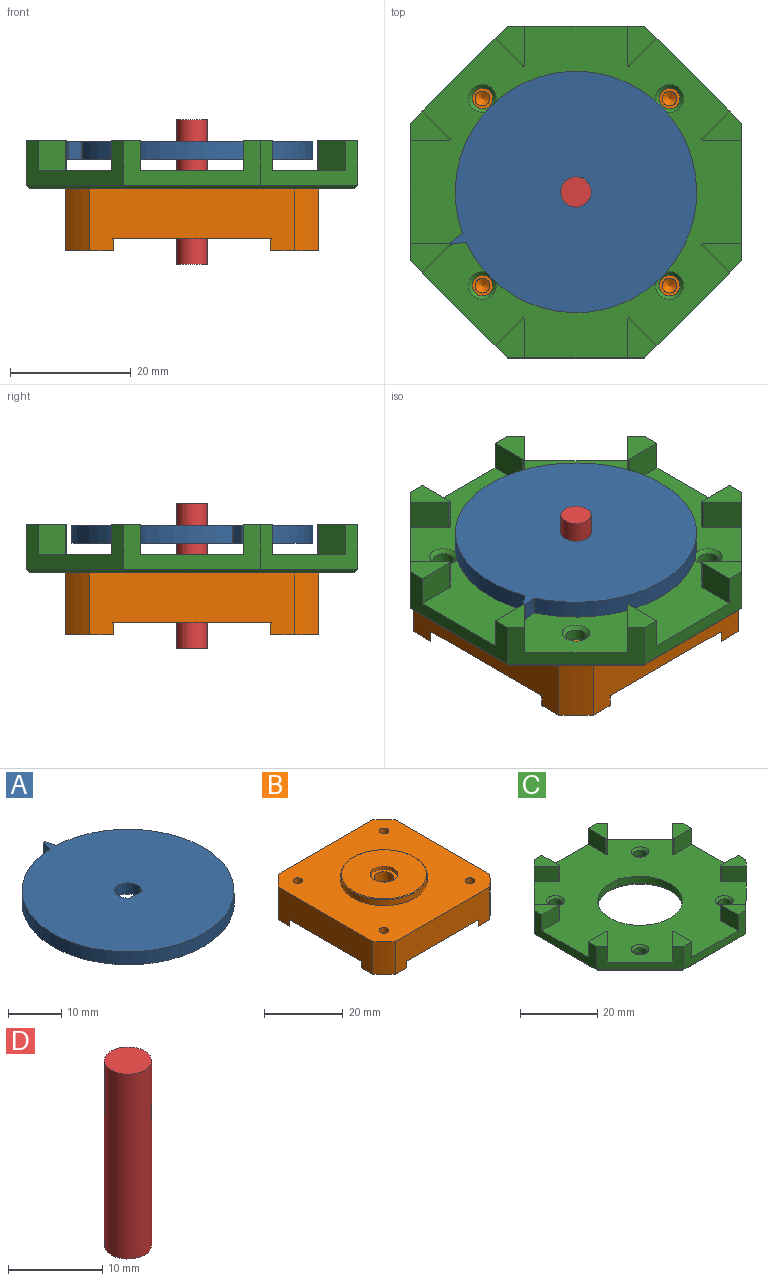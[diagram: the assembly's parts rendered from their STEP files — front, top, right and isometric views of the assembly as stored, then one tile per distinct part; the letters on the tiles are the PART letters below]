
ASSEMBLY  parts=4 mates=4
PART A: 14 faces, bbox 40x42.4x3 mm
  f0: plane 3x2.15mm, normal (0.97,0.26,0), area 6.7mm2, adj f6,f7,f8,f10
  f1: plane 3x2.15mm, normal (-0.97,0.26,0), area 6.7mm2, adj f6,f7,f8,f9
  f2: plane 3.23x2.4mm, normal (0,1,0), area 7.8mm2, adj f3,f4,f6,f11
  f3: cylinder r=2.5mm len=5mm, axis (0,0,-1), area 27.6mm2, adj f2,f4,f6,f12
  f4: plane 2.4x0.75mm, normal (-0.87,0.5,0), area 2.1mm2, adj f2,f3,f6,f13
  f5: cylinder r=20mm len=40mm, axis (0,0,-1), area 371.3mm2, adj f6,f7,f9,f10
  f6: plane 42.43x40mm, normal (0,0,1), area 1240.3mm2, adj f0,f1,f2,f3,f4,f5,f8,f9
  f7: plane 42.43x40mm, normal (0,0,-1), area 1229.8mm2, adj f0,f1,f5,f8,f9,f10,f11,f12
  f8: cylinder r=0.2mm len=3mm, axis (0,0,1), area 1.6mm2, adj f0,f1,f6,f7
  f9: cylinder r=0.2mm len=3mm, axis (0,0,-1), area 0.8mm2, adj f1,f5,f6,f7
  f10: cylinder r=0.2mm len=3mm, axis (0,0,-1), area 0.8mm2, adj f0,f5,f6,f7
  f11: plane 3.78x0.62mm, normal (0,0.71,-0.71), area 3mm2, adj f2,f7,f12,f13
  f12: cone r=3.1mm half-angle=45deg, axis (0,0,-1), area 11mm2, adj f3,f7,f11,f13
  f13: plane 1.35x0.95mm, normal (-0.61,0.35,-0.71), area 0.9mm2, adj f4,f7,f11,f12
PART B: 33 faces, bbox 42x42x12.2 mm
  f0: plane 8x8mm, normal (-0.71,0.71,0), area 22.6mm2, adj f4,f5,f9,f28
  f1: plane 8x8mm, normal (0.71,0.71,0), area 22.6mm2, adj f4,f8,f28,f30
  f2: plane 8x8mm, normal (0.71,-0.71,0), area 22.6mm2, adj f4,f7,f10,f30
  f3: plane 8x8mm, normal (-0.71,-0.71,0), area 22.6mm2, adj f4,f5,f6,f10
  f4: plane 42x42mm, normal (0,0,-1), area 1636mm2, adj f0,f1,f2,f3,f5,f10,f28,f30
  f5: plane 33.94x10.2mm, normal (1,0,0), area 294.2mm2, adj f0,f3,f4,f6,f9,f26,f27,f32
  f6: plane 8x8mm, normal (0,0,-1), area 24.5mm2, adj f3,f5,f10,f26
  f7: plane 8x8mm, normal (0,0,-1), area 24.5mm2, adj f2,f10,f30,f31
  f8: plane 8x8mm, normal (0,0,-1), area 24.5mm2, adj f1,f28,f29,f30
  f9: plane 8x8mm, normal (0,0,-1), area 24.5mm2, adj f0,f5,f27,f28
  f10: plane 33.94x10.2mm, normal (0,1,0), area 294.2mm2, adj f2,f3,f4,f6,f7,f26,f31,f32
  f11: cone r=10.9mm half-angle=45deg, axis (0,0,-1), area 19.4mm2, adj f12,f13
  f12: cylinder r=11mm len=22mm, axis (0,0,1), area 124.4mm2, adj f11,f32
  f13: plane 21.6x21.6mm, normal (0,0,1), area 328mm2, adj f11,f15
  f14: plane 7x7mm, normal (0,0,1), area 18.8mm2, adj f15,f16
  f15: cylinder r=3.5mm len=7mm, axis (0,0,1), area 22mm2, adj f13,f14
  f16: cylinder r=2.5mm len=5mm, axis (0,0,1), area 47.1mm2, adj f14,f17
  f17: plane 5x5mm, normal (0,0,1), area 19.6mm2, adj f16
  f18: cone r=0.61mm half-angle=59deg, axis (0,0,1), area 5.5mm2, adj f19
  f19: cylinder r=1.23mm len=2.5mm, axis (0,0,1), area 19.3mm2, adj f18,f32
  f20: cone r=0.61mm half-angle=59deg, axis (0,0,1), area 5.5mm2, adj f21
  f21: cylinder r=1.23mm len=2.5mm, axis (0,0,1), area 19.3mm2, adj f20,f32
  f22: cone r=0.61mm half-angle=59deg, axis (0,0,1), area 5.5mm2, adj f23
  f23: cylinder r=1.23mm len=2.5mm, axis (0,0,1), area 19.3mm2, adj f22,f32
  f24: cone r=0.61mm half-angle=59deg, axis (0,0,1), area 5.5mm2, adj f25
  f25: cylinder r=1.23mm len=2.5mm, axis (0,0,1), area 19.3mm2, adj f24,f32
  f26: cylinder r=27mm len=10.2mm, axis (0,0,1), area 58.2mm2, adj f5,f6,f10,f32
  f27: cylinder r=27mm len=10.2mm, axis (0,0,1), area 58.2mm2, adj f5,f9,f28,f32
  f28: plane 33.94x10.2mm, normal (0,-1,0), area 294.2mm2, adj f0,f1,f4,f8,f9,f27,f29,f32
  f29: cylinder r=27mm len=10.2mm, axis (0,0,1), area 58.2mm2, adj f8,f28,f30,f32
  f30: plane 33.94x10.2mm, normal (-1,0,0), area 294.2mm2, adj f1,f2,f4,f7,f8,f29,f31,f32
  f31: cylinder r=27mm len=10.2mm, axis (0,0,1), area 58.2mm2, adj f7,f10,f30,f32
  f32: plane 42x42mm, normal (0,0,1), area 1334.7mm2, adj f5,f10,f12,f19,f21,f23,f25,f26
PART C: 66 faces, bbox 55.3x55.3x8.3 mm
  f0: plane 55x55mm, normal (0,0,1), area 1899.9mm2, adj f2,f3,f4,f5,f6,f7,f8,f9
  f1: cone r=11.8mm half-angle=45deg, axis (0,0,-1), area 79.4mm2, adj f9,f11,f16,f17
  f2: plane 16.11x16.11mm, normal (0.71,-0.71,0), area 83.4mm2, adj f0,f3,f10,f22,f24,f27,f28,f56
  f3: plane 22.78x7.4mm, normal (1,0,0), area 83.4mm2, adj f0,f2,f4,f26,f28,f31,f32,f54
  f4: plane 16.11x16.11mm, normal (0.71,0.71,0), area 83.4mm2, adj f0,f3,f5,f30,f32,f35,f36,f52
  f5: plane 22.78x7.4mm, normal (0,1,0), area 83.4mm2, adj f0,f4,f6,f34,f36,f39,f40,f50
  f6: plane 16.11x16.11mm, normal (-0.71,0.71,0), area 83.4mm2, adj f0,f5,f7,f38,f40,f43,f44,f51
  f7: plane 22.78x7.4mm, normal (-1,0,0), area 83.4mm2, adj f0,f6,f8,f42,f44,f47,f48,f53
  f8: plane 16.11x16.11mm, normal (-0.71,-0.71,0), area 83.4mm2, adj f0,f7,f10,f19,f20,f46,f48,f55
  f9: cylinder r=11mm len=22mm, axis (0,0,-1), area 139.4mm2, adj f0,f1,f16,f17
  f10: plane 22.78x7.4mm, normal (0,-1,0), area 83.4mm2, adj f0,f2,f8,f18,f20,f23,f24,f57
  f11: plane 53.8x53.8mm, normal (0,0,-1), area 1893.9mm2, adj f1,f50,f51,f52,f53,f54,f55,f56
  f12: cylinder r=1.7mm len=3.4mm, axis (0,0,-1), area 19.2mm2, adj f61,f65
  f13: cylinder r=1.7mm len=3.4mm, axis (0,0,-1), area 19.2mm2, adj f59,f64
  f14: cylinder r=1.7mm len=3.4mm, axis (0,0,-1), area 19.2mm2, adj f58,f63
  f15: cylinder r=1.7mm len=3.4mm, axis (0,0,-1), area 19.2mm2, adj f60,f62
  f16: plane 3.24x2.87mm, normal (0,-1,0), area 6.9mm2, adj f0,f1,f9,f17
  f17: plane 2.86x2.83mm, normal (-0.5,-0.87,0), area 6.9mm2, adj f0,f1,f9,f16
  f18: plane 6.45x5mm, normal (1,0,0), area 32.2mm2, adj f0,f10,f20,f21
  f19: plane 5x4.56mm, normal (-0.71,0.71,0), area 32.2mm2, adj f0,f8,f20,f21
  f20: plane 6.65x4.9mm, normal (0,0,1), area 19.8mm2, adj f8,f10,f18,f19,f21
  f21: cylinder r=0.2mm len=5mm, axis (0,0,-1), area 2.4mm2, adj f0,f18,f19,f20
  f22: plane 5x4.56mm, normal (0.71,0.71,0), area 32.2mm2, adj f0,f2,f24,f25
  f23: plane 6.45x5mm, normal (-1,0,0), area 32.2mm2, adj f0,f10,f24,f25
  f24: plane 6.65x4.9mm, normal (0,0,1), area 19.8mm2, adj f2,f10,f22,f23,f25
  f25: cylinder r=0.2mm len=5mm, axis (0,0,-1), area 2.4mm2, adj f0,f22,f23,f24
  f26: plane 6.45x5mm, normal (0,1,0), area 32.2mm2, adj f0,f3,f28,f29
  f27: plane 5x4.56mm, normal (-0.71,-0.71,0), area 32.2mm2, adj f0,f2,f28,f29
  f28: plane 6.65x4.9mm, normal (0,0,1), area 19.8mm2, adj f2,f3,f26,f27,f29
  f29: cylinder r=0.2mm len=5mm, axis (0,0,-1), area 2.4mm2, adj f0,f26,f27,f28
  f30: plane 5x4.56mm, normal (-0.71,0.71,0), area 32.2mm2, adj f0,f4,f32,f33
  f31: plane 6.45x5mm, normal (0,-1,0), area 32.2mm2, adj f0,f3,f32,f33
  f32: plane 6.65x4.9mm, normal (0,0,1), area 19.8mm2, adj f3,f4,f30,f31,f33
  f33: cylinder r=0.2mm len=5mm, axis (0,0,-1), area 2.4mm2, adj f0,f30,f31,f32
  f34: plane 6.45x5mm, normal (-1,0,0), area 32.2mm2, adj f0,f5,f36,f37
  f35: plane 5x4.56mm, normal (0.71,-0.71,0), area 32.2mm2, adj f0,f4,f36,f37
  f36: plane 6.65x4.9mm, normal (0,0,1), area 19.8mm2, adj f4,f5,f34,f35,f37
  f37: cylinder r=0.2mm len=5mm, axis (0,0,-1), area 2.4mm2, adj f0,f34,f35,f36
  f38: plane 5x4.56mm, normal (-0.71,-0.71,0), area 32.2mm2, adj f0,f6,f40,f41
  f39: plane 6.45x5mm, normal (1,0,0), area 32.2mm2, adj f0,f5,f40,f41
  f40: plane 6.65x4.9mm, normal (0,0,1), area 19.8mm2, adj f5,f6,f38,f39,f41
  f41: cylinder r=0.2mm len=5mm, axis (0,0,-1), area 2.4mm2, adj f0,f38,f39,f40
  f42: plane 6.45x5mm, normal (0,-1,0), area 32.2mm2, adj f0,f7,f44,f45
  f43: plane 5x4.56mm, normal (0.71,0.71,0), area 32.2mm2, adj f0,f6,f44,f45
  f44: plane 6.65x4.9mm, normal (0,0,1), area 19.8mm2, adj f6,f7,f42,f43,f45
  f45: cylinder r=0.2mm len=5mm, axis (0,0,-1), area 2.4mm2, adj f0,f42,f43,f44
  f46: plane 5x4.56mm, normal (0.71,-0.71,0), area 32.2mm2, adj f0,f8,f48,f49
  f47: plane 6.45x5mm, normal (0,1,0), area 32.2mm2, adj f0,f7,f48,f49
  f48: plane 6.65x4.9mm, normal (0,0,1), area 19.8mm2, adj f7,f8,f46,f47,f49
  f49: cylinder r=0.2mm len=5mm, axis (0,0,-1), area 2.4mm2, adj f0,f46,f47,f48
  f50: plane 22.78x0.6mm, normal (0,0.71,-0.71), area 19.1mm2, adj f5,f11,f51,f52
  f51: plane 16.36x16.36mm, normal (-0.5,0.5,-0.71), area 19.1mm2, adj f6,f11,f50,f53
  f52: plane 16.36x16.36mm, normal (0.5,0.5,-0.71), area 19.1mm2, adj f4,f11,f50,f54
  f53: plane 22.78x0.6mm, normal (-0.71,0,-0.71), area 19.1mm2, adj f7,f11,f51,f55
  f54: plane 22.78x0.6mm, normal (0.71,0,-0.71), area 19.1mm2, adj f3,f11,f52,f56
  f55: plane 16.36x16.36mm, normal (-0.5,-0.5,-0.71), area 19.1mm2, adj f8,f11,f53,f57
  f56: plane 16.36x16.36mm, normal (0.5,-0.5,-0.71), area 19.1mm2, adj f2,f11,f54,f57
  f57: plane 22.78x0.6mm, normal (0,-0.71,-0.71), area 19.1mm2, adj f10,f11,f55,f56
  f58: cone r=2.3mm half-angle=45deg, axis (0,0,1), area 10.7mm2, adj f0,f14
  f59: cone r=2.3mm half-angle=45deg, axis (0,0,1), area 10.7mm2, adj f0,f13
  f60: cone r=2.3mm half-angle=45deg, axis (0,0,1), area 10.7mm2, adj f0,f15
  f61: cone r=2.3mm half-angle=45deg, axis (0,0,1), area 10.7mm2, adj f0,f12
  f62: cone r=1.7mm half-angle=45deg, axis (0,0,-1), area 10.7mm2, adj f11,f15
  f63: cone r=1.7mm half-angle=45deg, axis (0,0,-1), area 10.7mm2, adj f11,f14
  f64: cone r=1.7mm half-angle=45deg, axis (0,0,-1), area 10.7mm2, adj f11,f13
  f65: cone r=1.7mm half-angle=45deg, axis (0,0,-1), area 10.7mm2, adj f11,f12
PART D: 3 faces, bbox 5x5x24 mm
  f0: cylinder r=2.5mm len=24mm, axis (0,0,1), area 377mm2, adj f1,f2
  f1: plane 5x5mm, normal (0,0,-1), area 19.6mm2, adj f0
  f2: plane 5x5mm, normal (0,0,1), area 19.6mm2, adj f0
PLACE A rot(axis=(0,0,1),112.3deg) t=(-11.53,-6.81,23.16)mm
PLACE B t=(-11.53,-6.81,-5.08)mm fixed
PLACE C t=(-11.53,-6.81,18.27)mm
PLACE D t=(-11.53,-6.81,-17.58)mm
MATE cylindrical D.f0 <-> B.f11  axis (0,0,1) through (-11.53,-6.81,17.77)mm
MATE planar C.f1 <-> B.f11  axis (0,0,-1) through (-11.53,-6.81,18.27)mm
MATE cylindrical D.f0 <-> A.f3  axis (0,0,1) through (-11.53,-6.81,17.77)mm
MATE cylindrical C.f1 <-> B.f11  axis (0,0,-1) through (-11.53,-6.81,20.17)mm
